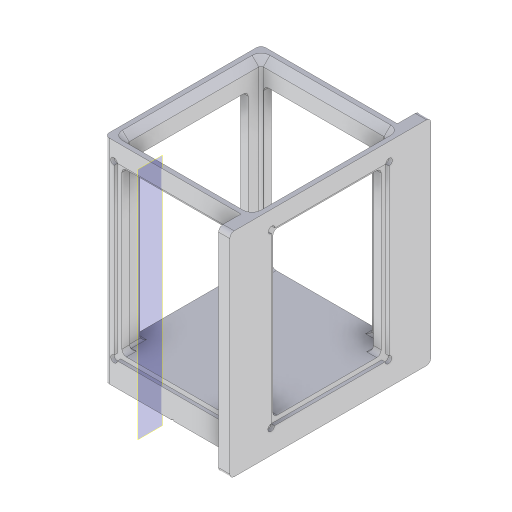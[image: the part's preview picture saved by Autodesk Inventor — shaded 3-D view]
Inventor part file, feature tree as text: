
AUTODESK INVENTOR PART (.ipt)
format: ipt  version: 2024 (Build 280153000, 153)  size: 373,760 bytes
history: native  units: mm
features: extrude x10, sketch x3, fillet x3, other x1, hole x1, chamfer x1, projected_geometry x1
ambient origin geometry x8: Origin, YZ Plane, XZ Plane, XY Plane, X Axis, Y Axis, Z Axis, Center Point
bodies: Solid1 (feature_tree)
feature tree (20):
  extrude  "Extrusion1"  Depth=70.0mm
  extrude  "Extrusion2"  Depth=10.0mm
  sketch  "Sketch12"  dims[d2=95.25mm d3=0.0mm d4=10.0mm]
  extrude  "Extrusion12"  Depth=2.0mm TaperAngle=0.0deg
  other  "LightSheet Plane1"
  sketch  "Sketch15"  dims[d5=10.0mm d6=5.0mm d7=0.0mm d57=2.0mm d58=8.0mm d59=2.0mm d60=3.0mm d61=3.0mm d62=3.0mm d63=3.0mm d64=0.0mm d65=0.0mm d73=35.6mm d84=8.0mm d85=2.0mm d86=2.0mm d87=3.0mm d88=3.0mm d89=3.0mm d90=3.0mm d91=0.0mm d92=0.0mm d93=1.5mm d94=0.0mm d95=5.0mm d96=5.0mm d97=5.0mm d98=0.0mm d99=20.0mm d100=0.0mm d101=1.0mm d102=1.5mm d103=0.0mm d104=2.0mm d105=1.5mm d106=0.0mm d107=1.5mm d108=0.0mm d109=5.588mm d110=8.0mm d111=4.0mm d112=2.0mm d113=90.0deg d114=10.0mm d115=20.594885mm d116=1.0mm d117=0.0mm d118=0.0mm d119=2.0mm d120=76.5mm d121=52.5mm d122=2.0mm d123=2.0mm d124=52.5mm d125=76.5mm d126=2.0mm d127=2.0mm d128=2.0mm d129=3.0mm d130=2.0mm d131=45.0deg d132=2.0mm]
  extrude  "Extrusion16"  Depth=2.0mm
  extrude  "Extrusion17"  Depth=2.0mm
  extrude  "Extrusion18"  Depth=2.0mm
  fillet  "Fillet2"  Radius=3.0mm
  extrude  "Extrusion19"  Depth=2.0mm
  fillet  "Fillet3"  Radius=3.0mm
  extrude  "Extrusion20"  Depth=2.0mm
  extrude  "Extrusion21"  TaperAngle=0.0deg  [1 undecoded]
  hole  "Hole2"  [1 undecoded]
  extrude  "Extrusion22"  Depth=2.0mm
  chamfer  "Chamfer1"  Distance=2.0mm
  fillet  "Fillet4"  Radius=2.0mm
  sketch  "Sketch2"  dims[d0=61.0mm d1=70.0mm]
  projected_geometry  "Projected Loop1"
note: 2 required parameter values undecoded (feature->parameter linkage not recoverable at this tier; creation-order binding heuristic only, values carry confidence <= 0.55)
